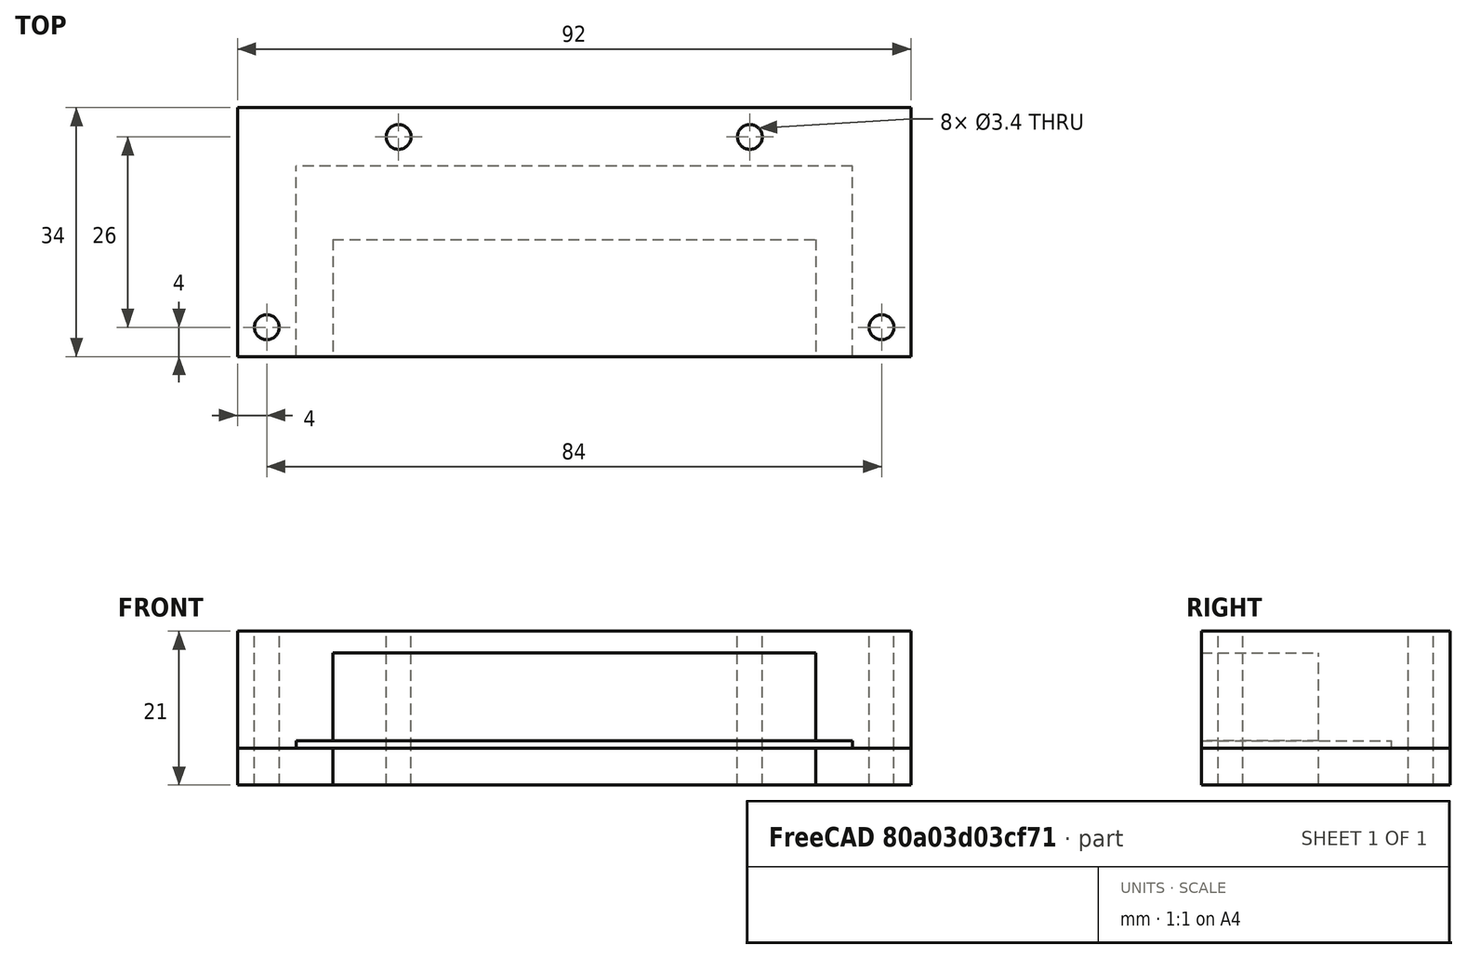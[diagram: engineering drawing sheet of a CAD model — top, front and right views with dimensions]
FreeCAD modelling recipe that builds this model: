
FCSTD DOCUMENT  (FreeCAD 0.16R6703 (Git))
Label: slide-mould
License: All rights reserved
LicenseURL: http://en.wikipedia.org/wiki/All_rights_reserved
objects: Part::Cylinder×8, Part::Box×5, Part::Cut×5, Part::MultiFuse×2
note: 20 computed .brp shape members not serialized (recipe doc carries the construction recipe); baked Part::Feature solids carry a one-line shape summary decoded from their .brp

FEATURE [Part::Box] Box  label="Cube"
  Height = 10
  Length = 76
  Placement = pos=(0,0,-9) rot=(0,0,1;0rad)
  Width = 26
FEATURE [Part::Box] Box001  label="Cube001"
  Height = 16
  Length = 92
  Placement = pos=(-8,0,0) rot=(0,0,1;0rad)
  Width = 34
FEATURE [Part::Box] Box002  label="Cube002"
  Height = 22
  Length = 66
  Placement = pos=(5,-5,-9) rot=(0,0,1;0rad)
  Width = 21
FEATURE [Part::Cut] Cut
  Base = -> Box001
  Tool = -> Box002
FEATURE [Part::Cut] Cut001
  Base = -> Cut
  Placement = pos=(8,0,0) rot=(0,0,1;0rad)
  Tool = -> Box
FEATURE [Part::Box] Box003  label="Cube003"
  Height = 5
  Length = 92
  Placement = pos=(-8,0,-5) rot=(0,0,1;0rad)
  Width = 34
FEATURE [Part::Box] Box004  label="Cube004"
  Height = 22
  Length = 66
  Placement = pos=(5,-5,-9) rot=(0,0,1;0rad)
  Width = 21
FEATURE [Part::Cut] Cut002
  Base = -> Box003
  Placement = pos=(8,0,0) rot=(0,0,1;0rad)
  Tool = -> Box004
FEATURE [Part::Cylinder] Cylinder
  Angle = 360
  Height = 25
  Placement = pos=(4,4,-7) rot=(0,0,1;0rad)
  Radius = 1.7
FEATURE [Part::Cylinder] Cylinder001
  Angle = 360
  Height = 25
  Placement = pos=(88,4,-7) rot=(0,0,1;0rad)
  Radius = 1.7
FEATURE [Part::Cylinder] Cylinder002
  Angle = 360
  Height = 25
  Placement = pos=(22,30,-7) rot=(0,0,1;0rad)
  Radius = 1.7
FEATURE [Part::Cylinder] Cylinder003
  Angle = 360
  Height = 25
  Placement = pos=(70,30,-7) rot=(0,0,1;0rad)
  Radius = 1.7
FEATURE [Part::Cylinder] Cylinder004
  Angle = 360
  Height = 25
  Placement = pos=(4,4,-7) rot=(0,0,1;0rad)
  Radius = 1.7
FEATURE [Part::Cylinder] Cylinder005
  Angle = 360
  Height = 25
  Placement = pos=(70,30,-7) rot=(0,0,1;0rad)
  Radius = 1.7
FEATURE [Part::Cylinder] Cylinder006
  Angle = 360
  Height = 25
  Placement = pos=(22,30,-7) rot=(0,0,1;0rad)
  Radius = 1.7
FEATURE [Part::Cylinder] Cylinder007
  Angle = 360
  Height = 25
  Placement = pos=(88,4,-7) rot=(0,0,1;0rad)
  Radius = 1.7
FEATURE [Part::MultiFuse] Fusion
  Shapes = -> [Cylinder,Cylinder003,Cylinder002,Cylinder001]
FEATURE [Part::MultiFuse] Fusion001
  Shapes = -> [Cylinder004,Cylinder006,Cylinder005,Cylinder007]
FEATURE [Part::Cut] Cut003
  Base = -> Cut001
  Tool = -> Fusion
FEATURE [Part::Cut] Cut004
  Base = -> Cut002
  Tool = -> Fusion001
